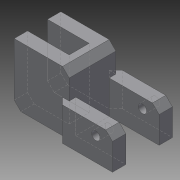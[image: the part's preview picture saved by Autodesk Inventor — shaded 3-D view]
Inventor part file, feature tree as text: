
AUTODESK INVENTOR PART (.ipt)
format: ipt  version: 2015 (Build 190159000, 159)  size: 133,632 bytes
history: native  units: mm
features: chamfer x4, extrude x3, sketch x3
ambient origin geometry x8: Origin, YZ Plane, XZ Plane, XY Plane, X Axis, Y Axis, Z Axis, Center Point
bodies: Solid1 (feature_tree)
feature tree (10):
  extrude  "Extrusion1"  Depth=6.0mm
  extrude  "Extrusion2"  Depth=4.0mm
  chamfer  "Chamfer1"  Distance=18.0mm
  chamfer  "Chamfer2"  Distance=10.0mm
  extrude  "Extrusion3"  Depth=10.0mm
  chamfer  "Chamfer3"  Distance=2.0mm
  chamfer  "Chamfer4"  Distance=2.0mm
  sketch  "Sketch1"  dims[d0=12.5mm d1=6.0mm]
  sketch  "Sketch2"  dims[d2=4.0mm d3=4.0mm]
  sketch  "Sketch3"  dims[d4=4.0mm d5=18.0mm d6=0.0mm d7=10.0mm d8=10.0mm d9=2.0mm d10=2.0mm d11=4.0mm d12=4.0mm d13=15.0mm d14=0.0mm d15=2.0mm d16=2.0mm d17=45.0deg d18=2.0mm d19=2.0mm d20=45.0deg d21=3.0mm d22=5.0mm d23=2.5mm d24=30.0mm d25=0.0mm d26=2.0mm d27=2.0mm d28=45.0deg d29=2.0mm d30=2.0mm d31=45.0deg]
